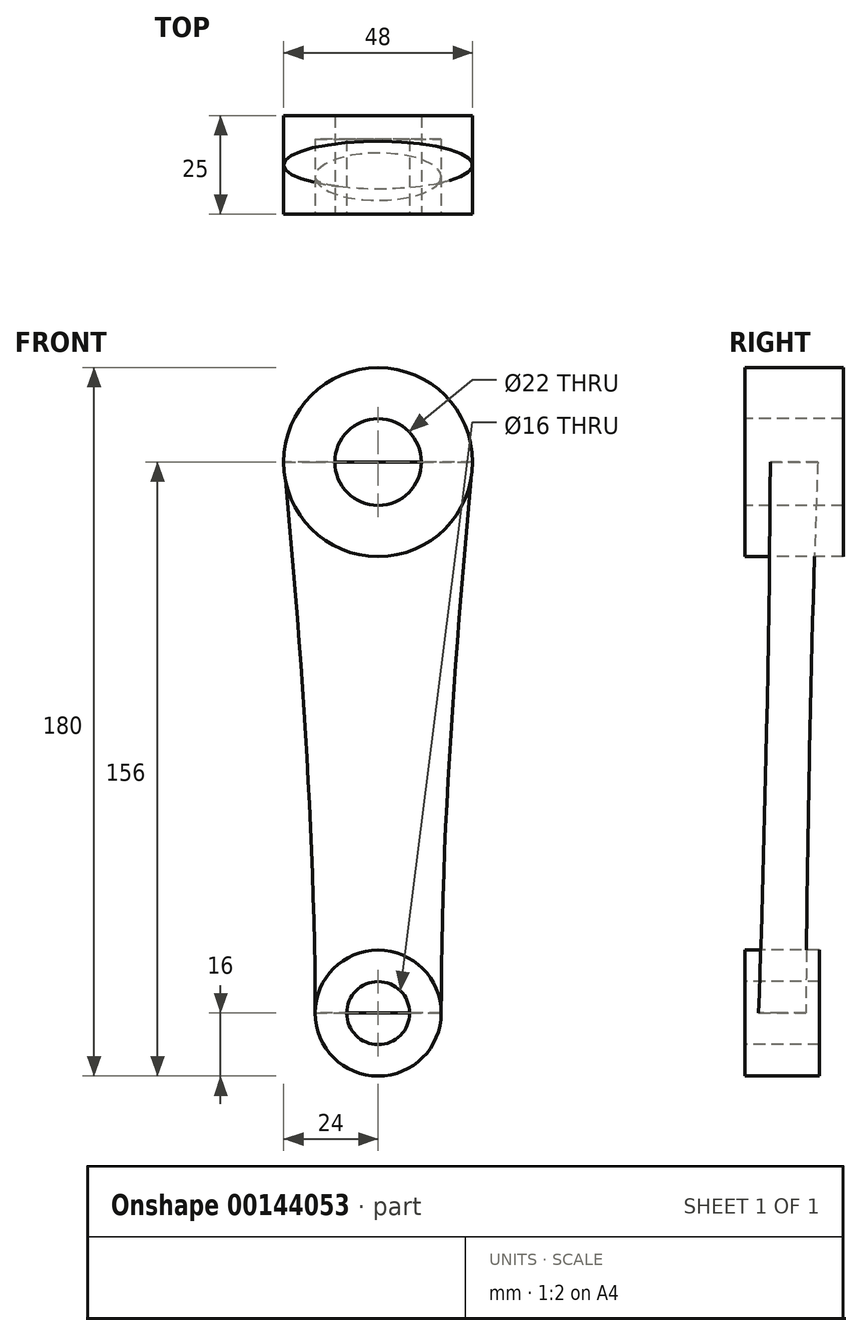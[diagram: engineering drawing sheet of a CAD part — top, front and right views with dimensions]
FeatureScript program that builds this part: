
annotation { "Feature Type Name" : "Feature", "Feature Type Description" : "" }
export const myFeature = defineFeature(function(context is Context, id is Id, definition is map)
    precondition{}
    {
        {
            var Q0;
            Q0=qCreatedBy(makeId("Front.planeOp"),FACE);
            var sketch = newSketch(context, id + "F0", { "sketchPlane" : qUnion([Q0])});
            skCircle(sketch, "E0", {"center": v(0, 0) * mm, "radius": 8 * mm});
            skCircle(sketch, "E1", {"center": v(0, 0) * mm, "radius": 16 * mm});
            skCircle(sketch, "E2", {"center": v(0, 140) * mm, "radius": 11 * mm});
            skCircle(sketch, "E3", {"center": v(0, 140) * mm, "radius": 24 * mm});
            skSolve(sketch);
        }
        {
            var Q0;
            Q0=makeQuery(id+"F0.imprint","IMPRINT",FACE,{"disambiguationData":[TD([[makeQuery(id+"F0.imprint","IMPRINT",EDGE,{"derivedFrom":sQuery(id+"F0.wireOp",EDGE,"E0")}),-1.0]])]});
            extrude(context, id + "F1", {"entities" : qUnion([Q0]), "oppositeDirection" : true, "depth" : 19 * mm});
        }
        {
            var Q0;
            Q0=qCreatedBy(makeId("Top.planeOp"),FACE);
            var sketch = newSketch(context, id + "F2", { "sketchPlane" : qUnion([Q0])});
            skEllipse(sketch, "E4", {"center": v(0, 9.5) * mm, "majorRadius": 16 * mm, "minorRadius": 6 * mm, "majorAxis": v(-1, 0)});
            skSolve(sketch);
        }
        {
            var Q0;
            Q0=makeQuery(id+"F0.imprint","IMPRINT",FACE,{"disambiguationData":[TD([[makeQuery(id+"F0.imprint","IMPRINT",EDGE,{"derivedFrom":sQuery(id+"F0.wireOp",EDGE,"E2")}),-1.0]])]});
            extrude(context, id + "F3", {"entities" : qUnion([Q0]), "oppositeDirection" : true, "depth" : 25 * mm});
        }
        {
            var Q0;
            Q0=qCreatedBy(makeId("Top.planeOp"),FACE);
            var Q1;
            Q1=sQuery(id+"F0.wireOp",VERTEX,"E3.center");
            cPlane(context, id + "F4", {"entities" : qUnion([Q0, Q1]), "cplaneType" : CPlaneType.PLANE_POINT, "offset" : 25 * mm, "width" : 150 * mm, "height" : 150 * mm});
        }
        {
            var Q0;
            Q0=qCreatedBy(id+"F4.planeOp",FACE);
            var sketch = newSketch(context, id + "F5", { "sketchPlane" : qUnion([Q0])});
            skEllipse(sketch, "E5", {"center": v(0, 12.5) * mm, "majorRadius": 24 * mm, "minorRadius": 6 * mm, "majorAxis": v(-1, 0)});
            skSolve(sketch);
        }
        {
            var Q0;
            Q0 = qSketchRegion(id + "F2", true);
            var Q1;
            Q1 = qSketchRegion(id + "F5", true);
            loft(context, id + "F6", {"sheetProfilesArray" : [{ "sheetProfileEntities" : qUnion([Q0]) }, { "sheetProfileEntities" : qUnion([Q1]) }]});
        }
    });
